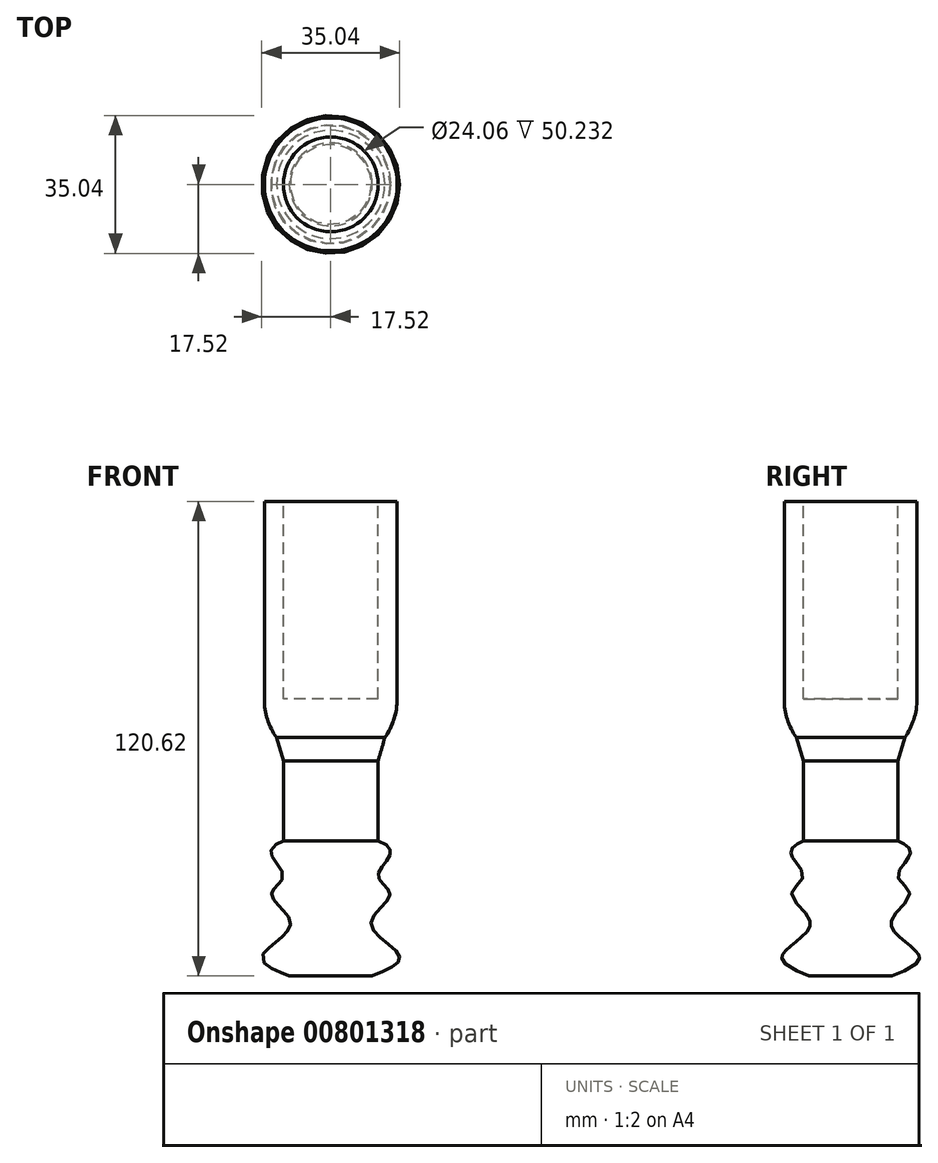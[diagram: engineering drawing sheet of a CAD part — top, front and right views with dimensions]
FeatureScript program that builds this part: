
annotation { "Feature Type Name" : "Feature", "Feature Type Description" : "" }
export const myFeature = defineFeature(function(context is Context, id is Id, definition is map)
    precondition{}
    {
        {
            var Q0;
            Q0=qCreatedBy(makeId("Front.planeOp"),FACE);
            var sketch = newSketch(context, id + "F0", { "sketchPlane" : qUnion([Q0])});
            skArc(sketch, "E0", {"start": v(-24.3, 11.72) * mm, "mid": v(-21.98, 16.37) * mm, "end": v(-21.18, 21.5) * mm});
            skLineSegment(sketch, "E1", {"start": v(-21.18, 21.5) * mm, "end": v(-21.18, 71.74) * mm});
            skLineSegment(sketch, "E2", {"start": v(-21.18, 71.74) * mm, "end": v(-26.02, 71.74) * mm});
            skLineSegment(sketch, "E3", {"start": v(-26.02, 71.74) * mm, "end": v(-26.02, 21.5) * mm});
            skLineSegment(sketch, "E4", {"start": v(-26.02, 21.5) * mm, "end": v(-38.05, 21.5) * mm});
            skLineSegment(sketch, "E5", {"start": v(-24.3, 11.72) * mm, "end": v(-26.02, 5.72) * mm});
            skLineSegment(sketch, "E6", {"start": v(-26.02, 5.72) * mm, "end": v(-26.02, -14.59) * mm});
            skFitSpline(sketch, "E7", {"points": [v(-26.02, -14.59) * mm, v(-23.01, -18.2) * mm, v(-26.02, -23.61) * mm, v(-23.01, -28.12) * mm, v(-27.82, -35.64) * mm, v(-20.6, -43.76) * mm, v(-27.52, -48.88) * mm], "startDerivative": vector(60.84, -21.62) * mm, "endDerivative": vector(-64, -26.27) * mm});
            skLineSegment(sketch, "E8", {"start": v(-38.05, 21.5) * mm, "end": v(-38.05, -48.88) * mm});
            skLineSegment(sketch, "E9", {"start": v(-38.05, -48.88) * mm, "end": v(-27.52, -48.88) * mm});
            skSolve(sketch);
        }
        {
            var Q0;
            Q0=makeQuery(id+"F0.imprint","IMPRINT",FACE,{"disambiguationData":[TD([[makeQuery(id+"F0.imprint","IMPRINT",EDGE,{"derivedFrom":sQuery(id+"F0.wireOp",EDGE,"E0")}),1.0]])]});
            var Q1;
            Q1=sQuery(id+"F0.wireOp",EDGE,"E8");
            revolve(context, id + "F1", {"surfaceOperationType" : NewSurfaceOperationType.NEW, "entities" : qUnion([Q0]), "axis" : qUnion([Q1]), "revolveType" : RevolveType.FULL});
        }
    });
